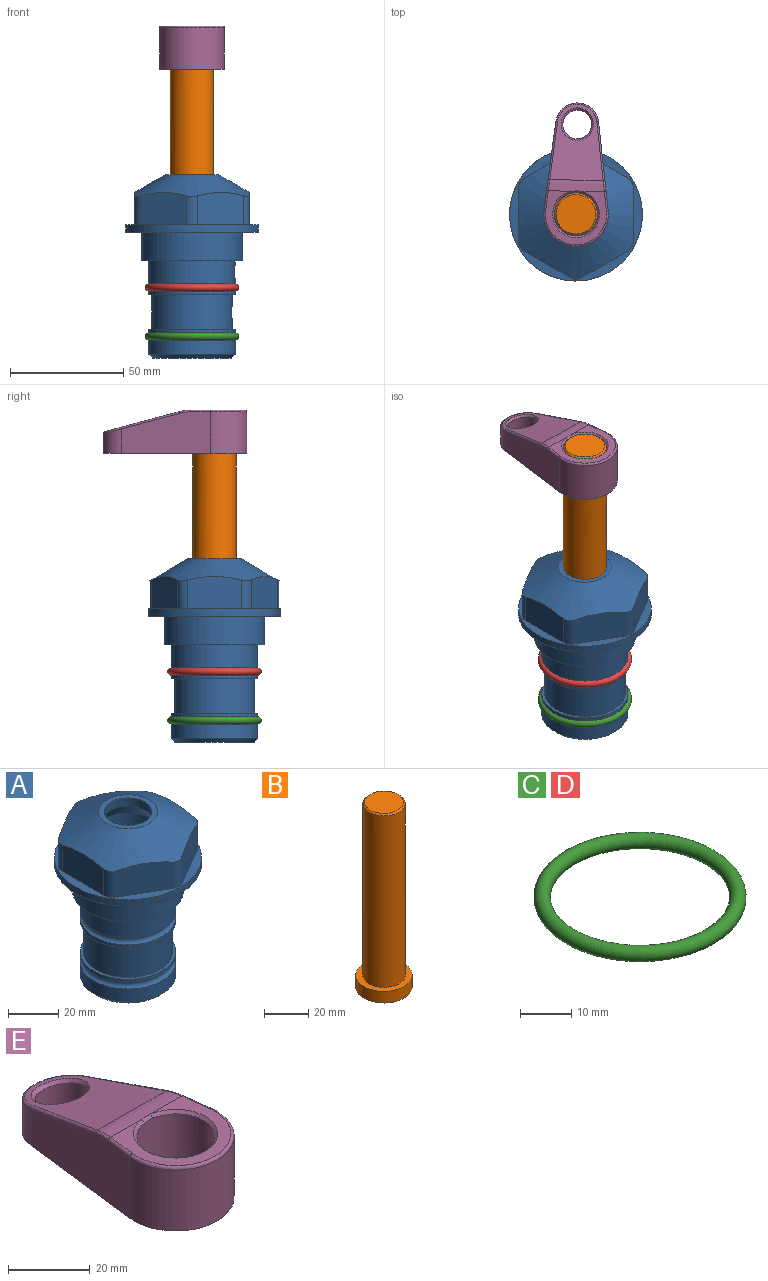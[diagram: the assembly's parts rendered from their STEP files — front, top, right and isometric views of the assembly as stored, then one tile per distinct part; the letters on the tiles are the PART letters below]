
ASSEMBLY  parts=5 mates=4
PART A: 36 faces, bbox 58.7x58.7x81 mm
  f0: cylinder r=17.78mm len=35.56mm, axis (0,0,1), area 1670.8mm2, adj f23,f24,f31
  f1: cylinder r=19.05mm len=38.1mm, axis (0,0,1), area 1191.9mm2, adj f26,f27,f30
  f2: plane 58.66x58.66mm, normal (0,0,-1), area 1150.6mm2, adj f3,f28
  f3: cylinder r=29.33mm len=58.66mm, axis (0,0,-1), area 585.1mm2, adj f2,f4
  f4: plane 58.66x58.66mm, normal (0,0,1), area 475.9mm2, adj f3,f5,f6,f7,f8,f9,f10,f11
  f5: plane 20.32x14.34mm, normal (-0.5,0.87,0), area 324.4mm2, adj f4,f15,f16,f17
  f6: plane 20.32x14.34mm, normal (0.5,0.87,0), area 324.4mm2, adj f4,f14,f15,f17
  f7: plane 23.48x14.34mm, normal (1,0,0), area 324.4mm2, adj f4,f13,f14,f17
  f8: plane 20.32x14.34mm, normal (0.5,-0.87,0), area 324.4mm2, adj f4,f12,f13,f17
  f9: plane 20.32x14.34mm, normal (-0.5,-0.87,0), area 324.4mm2, adj f4,f11,f12,f17
  f10: plane 23.48x14.34mm, normal (-1,0,0), area 324.4mm2, adj f4,f11,f16,f17
  f11: cylinder r=5.08mm len=12.85mm, axis (0,0,-1), area 67.2mm2, adj f4,f9,f10,f17
  f12: cylinder r=5.08mm len=12.85mm, axis (0,0,-1), area 67.2mm2, adj f4,f8,f9,f17
  f13: cylinder r=5.08mm len=12.85mm, axis (0,0,-1), area 67.2mm2, adj f4,f7,f8,f17
  f14: cylinder r=5.08mm len=12.85mm, axis (0,0,-1), area 67.2mm2, adj f4,f6,f7,f17
  f15: cylinder r=5.08mm len=12.85mm, axis (0,0,-1), area 67.2mm2, adj f4,f5,f6,f17
  f16: cylinder r=5.08mm len=12.85mm, axis (0,0,-1), area 67.2mm2, adj f4,f5,f10,f17
  f17: cone r=11.73mm half-angle=60deg, axis (0,0,-1), area 2071.8mm2, adj f5,f6,f7,f8,f9,f10,f11,f12
  f18: plane 23.46x23.46mm, normal (0,0,1), area 147.4mm2, adj f17,f35
  f19: plane 34.93x34.93mm, normal (0,0,-1), area 958mm2, adj f29
  f20: cylinder r=19.05mm len=38.1mm, axis (0,0,1), area 760.1mm2, adj f21,f29
  f21: torus R=19.05mm, axis (0,0,1), area 565.3mm2, adj f20,f22
  f22: cylinder r=19.05mm len=38.1mm, axis (0,0,1), area 190mm2, adj f21,f23
  f23: plane 38.1x38.1mm, normal (0,0,1), area 146.9mm2, adj f0,f22
  f24: plane 38.1x38.1mm, normal (0,0,-1), area 146.9mm2, adj f0,f25
  f25: cylinder r=19.05mm len=38.1mm, axis (0,0,1), area 190mm2, adj f24,f26
  f26: torus R=19.05mm, axis (0,0,1), area 565.3mm2, adj f1,f25
  f27: plane 44.45x44.45mm, normal (0,0,-1), area 411.7mm2, adj f1,f28
  f28: cylinder r=22.23mm len=44.45mm, axis (0,0,1), area 1773.5mm2, adj f2,f27
  f29: cone r=19.05mm half-angle=45deg, axis (0,0,1), area 257.5mm2, adj f19,f20
  f30: cylinder r=3.17mm len=6.75mm, axis (-1,0,0), area 128mm2, adj f1,f33
  f31: cylinder r=3.17mm len=6.35mm, axis (-1,0,0), area 102.5mm2, adj f0,f33
  f32: plane 25.4x25.4mm, normal (0,0,1), area 506.7mm2, adj f33
  f33: cylinder r=12.7mm len=66.42mm, axis (0,0,-1), area 5236.2mm2, adj f30,f31,f32,f34
  f34: cone r=9.53mm half-angle=30deg, axis (0,0,-1), area 443.4mm2, adj f33,f35
  f35: cylinder r=9.53mm len=19.05mm, axis (0,0,-1), area 240.9mm2, adj f18,f34
PART B: 6 faces, bbox 25.4x25.4x101.6 mm
  f0: plane 17.46x17.46mm, normal (0,0,1), area 239.5mm2, adj f5
  f1: plane 25.4x25.4mm, normal (0,0,-1), area 506.7mm2, adj f2
  f2: cylinder r=12.7mm len=25.4mm, axis (0,0,1), area 506.7mm2, adj f1,f3
  f3: plane 25.4x25.4mm, normal (0,0,1), area 221.7mm2, adj f2,f4
  f4: cylinder r=9.53mm len=94.46mm, axis (0,0,1), area 5653mm2, adj f3,f5
  f5: cone r=8.73mm half-angle=45deg, axis (0,0,-1), area 64.4mm2, adj f0,f4
PART C: 1 faces, bbox 44.7x44.7x3.2 mm
  f0: torus R=19.05mm, axis (0,0,1), area 1193.9mm2
PART D: same geometry as C
PART E: 31 faces, bbox 31.7x65.5x19.8 mm
  f0: plane 39.12x18.26mm, normal (0.99,0.12,0), area 612.2mm2, adj f1,f4,f7,f11,f13,f15
  f1: cylinder r=9.53mm len=18.91mm, axis (0,0,-1), area 296.1mm2, adj f0,f2,f7,f17
  f2: plane 39.12x18.26mm, normal (-0.99,0.12,0), area 612.2mm2, adj f1,f4,f7,f12,f14,f16
  f3: cylinder r=6.35mm len=12.7mm, axis (0,0,-1), area 362.4mm2, adj f7,f18
  f4: cylinder r=14.29mm len=28.58mm, axis (0,0,-1), area 882.2mm2, adj f0,f2,f7,f10
  f5: cylinder r=9.53mm len=19.05mm, axis (0,0,-1), area 1092.6mm2, adj f7,f19,f20
  f6: plane 26.99x23.69mm, normal (0,0,1), area 216.2mm2, adj f9,f10,f11,f12,f19
  f7: plane 63.5x28.58mm, normal (0,0,-1), area 661.8mm2, adj f0,f1,f2,f3,f4,f5,f22,f23
  f8: plane 33.52x23.6mm, normal (0,0.26,0.97), area 486mm2, adj f9,f15,f16,f17,f18
  f9: cylinder r=19.05mm len=24.72mm, axis (1,0,0), area 120.4mm2, adj f6,f8,f13,f14,f20
  f10: torus R=13.49mm, axis (0,0,1), area 59mm2, adj f4,f6,f11,f12
  f11: cylinder r=0.79mm len=8.67mm, axis (0.12,-0.99,0), area 10.8mm2, adj f0,f6,f10,f13
  f12: cylinder r=0.79mm len=8.67mm, axis (0.12,0.99,0), area 10.8mm2, adj f2,f6,f10,f14
  f13: bspline ~4.95x1.42mm, area 6.1mm2, adj f0,f9,f11,f15
  f14: bspline ~4.95x1.42mm, area 6.1mm2, adj f2,f9,f12,f16
  f15: cylinder r=0.79mm len=25.95mm, axis (0.12,-0.96,0.26), area 32.9mm2, adj f0,f8,f13,f17
  f16: cylinder r=0.79mm len=25.95mm, axis (0.12,0.96,-0.26), area 32.9mm2, adj f2,f8,f14,f17
  f17: bspline ~18.91x8.38mm, area 30mm2, adj f1,f8,f15,f16
  f18: bspline ~14.29x14.29mm, area 48.3mm2, adj f3,f8
  f19: cone r=9.53mm half-angle=45deg, axis (0,0,1), area 66.5mm2, adj f5,f6,f20
  f20: bspline ~3.22x0.96mm, area 3.5mm2, adj f5,f9,f19
  f21: plane 2.75x2.72mm, normal (0,0,-1), area 2.9mm2, adj f23,f25,f28
  f22: plane 23.05x15.88mm, normal (-0.99,-0.12,0), area 323.6mm2, adj f7,f25,f26,f27,f28,f29
  f23: plane 23.05x15.88mm, normal (0.99,-0.12,0), area 323.6mm2, adj f7,f21,f25,f27,f28,f30
  f24: cylinder r=9.53mm len=10.69mm, axis (0,0,-1), area 114.7mm2, adj f7,f27,f29,f30
  f25: cylinder r=12.7mm len=20.59mm, axis (0,0,-1), area 381.1mm2, adj f7,f21,f22,f23,f26,f28
  f26: plane 2.75x2.72mm, normal (0,0,-1), area 2.9mm2, adj f22,f25,f28
  f27: plane 19.72x18.37mm, normal (0,-0.26,-0.97), area 291.8mm2, adj f22,f23,f24,f28,f29,f30
  f28: cylinder r=15.88mm len=19.92mm, axis (1,0,0), area 54.8mm2, adj f21,f22,f23,f25,f26,f27
  f29: cylinder r=1.59mm len=11mm, axis (0,0,-1), area 34.7mm2, adj f7,f22,f24,f27
  f30: cylinder r=1.59mm len=11mm, axis (0,0,-1), area 34.7mm2, adj f7,f23,f24,f27
PLACE A at identity fixed
PLACE B rot(axis=(0,0,-1),0.8deg) t=(0,0,27.55)mm
PLACE C t=(0,0,-21.59)mm
PLACE D at identity
PLACE E rot(axis=(0,0,-1),0.8deg) t=(0,0,27.55)mm
MATE fastened E.f4 <-> B.f2  axis (0,0,1) through (0,0,91.05)mm
MATE fastened C.f0 <-> A.f0  axis (0,0,1) through (0,0,-46.1)mm
MATE cylindrical A.f0 <-> B.f2  axis (0,0,1) through (0,0,-50.55)mm
MATE fastened D.f0 <-> A.f0  axis (0,0,1) through (0,0,-24.51)mm
